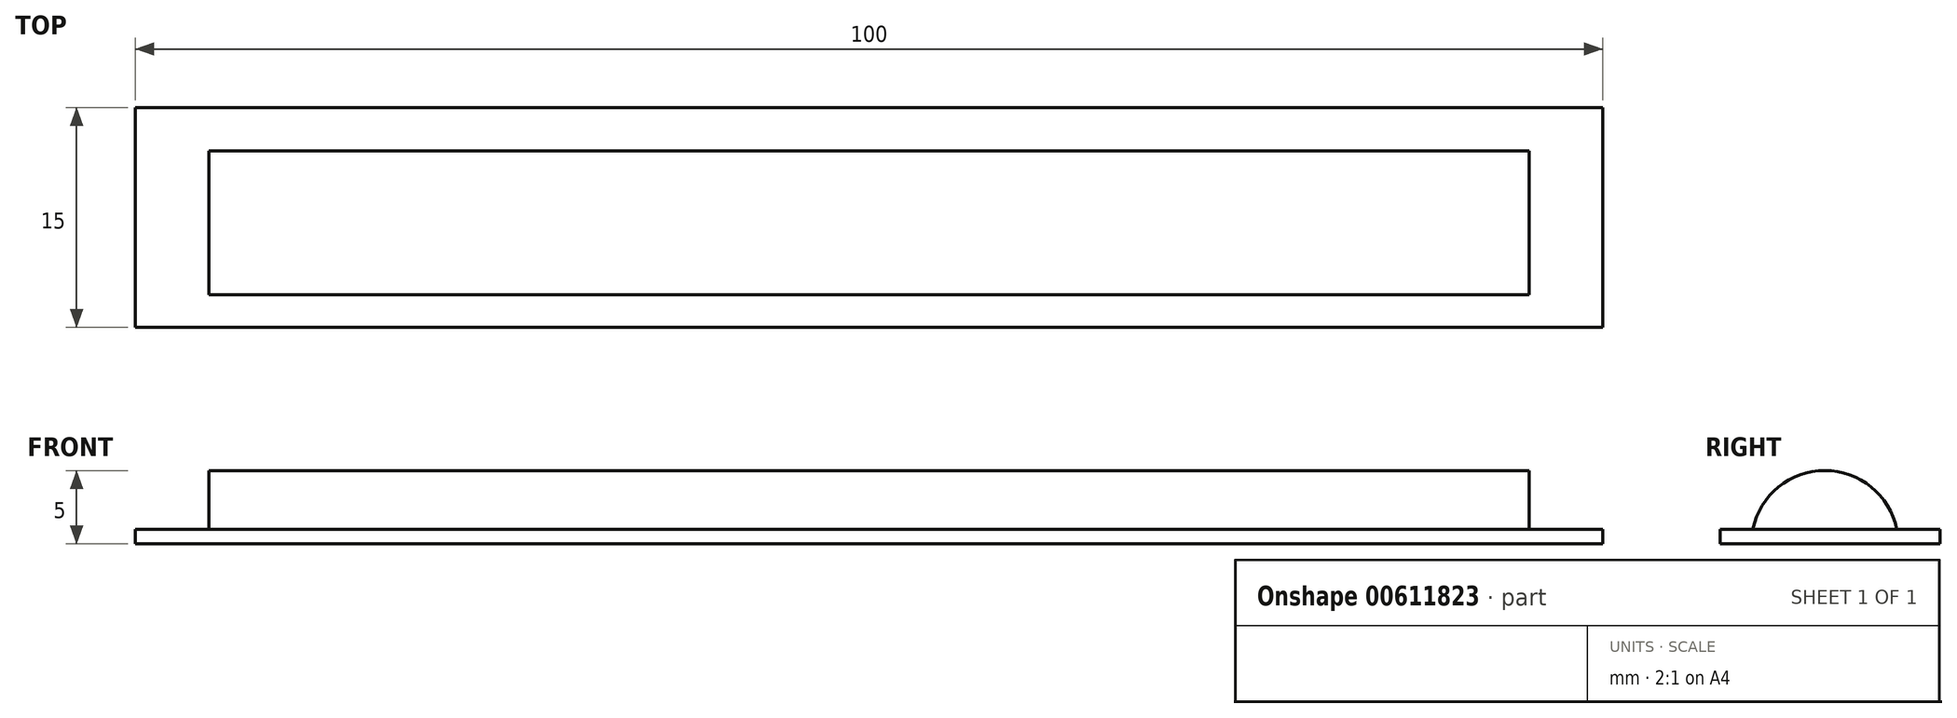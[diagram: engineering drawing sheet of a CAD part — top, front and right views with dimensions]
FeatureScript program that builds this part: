
annotation { "Feature Type Name" : "Feature", "Feature Type Description" : "" }
export const myFeature = defineFeature(function(context is Context, id is Id, definition is map)
    precondition{}
    {
        {
            var Q0;
            Q0=qCreatedBy(makeId("Top.planeOp"),FACE);
            var sketch = newSketch(context, id + "F0", { "sketchPlane" : qUnion([Q0])});
            skLineSegment(sketch, "E0.bottom", {"start": v(50, -7.5) * mm, "end": v(-50, -7.5) * mm});
            skLineSegment(sketch, "E0.top", {"start": v(50, 7.5) * mm, "end": v(-50, 7.5) * mm});
            skLineSegment(sketch, "E0.left", {"start": v(50, -7.5) * mm, "end": v(50, 7.5) * mm});
            skLineSegment(sketch, "E0.right", {"start": v(-50, -7.5) * mm, "end": v(-50, 7.5) * mm});
            skPoint(sketch, "E0.middle", {"position": v(0, 0) * mm});
            skSolve(sketch);
        }
        {
            var Q0;
            Q0 = qSketchRegion(id + "F0", true);
            extrude(context, id + "F1", {"entities" : qUnion([Q0]), "depth" : 1 * mm, "offsetDistance" : 25 * mm});
        }
        {
            var Q0;
            Q0=qCreatedBy(makeId("Top.planeOp"),FACE);
            var sketch = newSketch(context, id + "F2", { "sketchPlane" : qUnion([Q0])});
            skLineSegment(sketch, "E1.bottom", {"start": v(45, -5.36) * mm, "end": v(-45, -5.36) * mm});
            skLineSegment(sketch, "E1.top", {"start": v(45, -0.36) * mm, "end": v(-45, -0.36) * mm});
            skLineSegment(sketch, "E1.left", {"start": v(45, -5.36) * mm, "end": v(45, -0.36) * mm});
            skLineSegment(sketch, "E1.right", {"start": v(-45, -5.36) * mm, "end": v(-45, -0.36) * mm});
            skPoint(sketch, "E1.middle", {"position": v(0, -2.86) * mm});
            skSolve(sketch);
        }
        {
            var Q0;
            Q0 = qSketchRegion(id + "F2", true);
            var Q1;
            Q1=sQuery(id+"F2.wireOp",EDGE,"E1.top");
            revolve(context, id + "F3", {"operationType" : NewBodyOperationType.ADD, "entities" : qUnion([Q0]), "axis" : qUnion([Q1]), "revolveType" : RevolveType.ONE_DIRECTION, "angle" : 180 * degree});
        }
    });
